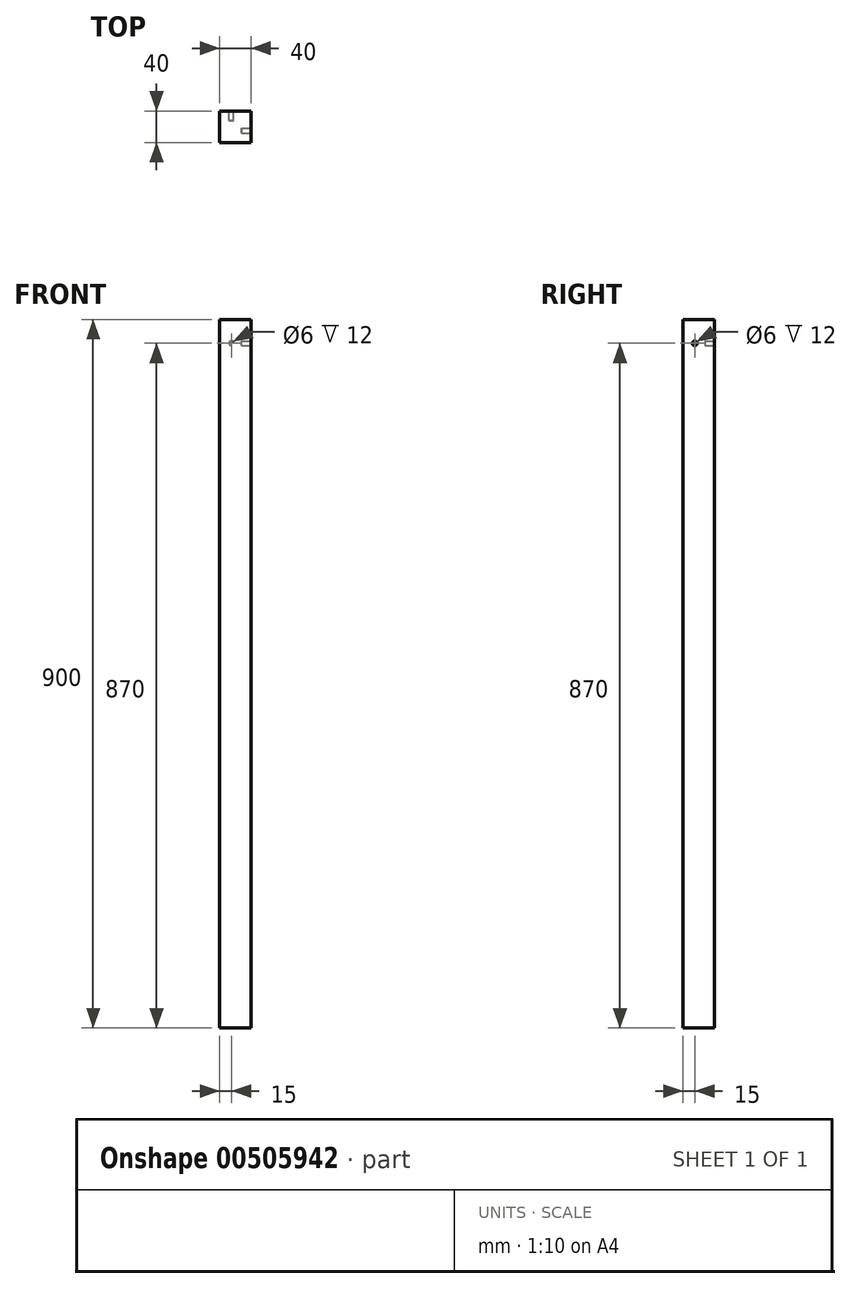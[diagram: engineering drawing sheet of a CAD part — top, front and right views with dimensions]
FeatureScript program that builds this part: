
annotation { "Feature Type Name" : "Feature", "Feature Type Description" : "" }
export const myFeature = defineFeature(function(context is Context, id is Id, definition is map)
    precondition{}
    {
        {
            var Q0;
            Q0=qCreatedBy(makeId("Top.planeOp"),FACE);
            var sketch = newSketch(context, id + "F0", { "sketchPlane" : qUnion([Q0])});
            skLineSegment(sketch, "E0.bottom", {"start": v(0, 0) * mm, "end": v(40, 0) * mm});
            skLineSegment(sketch, "E0.top", {"start": v(0, 40) * mm, "end": v(40, 40) * mm});
            skLineSegment(sketch, "E0.left", {"start": v(0, 0) * mm, "end": v(0, 40) * mm});
            skLineSegment(sketch, "E0.right", {"start": v(40, 0) * mm, "end": v(40, 40) * mm});
            skSolve(sketch);
        }
        {
            var Q0;
            Q0=makeQuery(id+"F0.imprint","IMPRINT",FACE,{"disambiguationData":[TD([[makeQuery(id+"F0.imprint","IMPRINT",EDGE,{"derivedFrom":sQuery(id+"F0.wireOp",EDGE,"E0.bottom")}),1.0]])]});
            extrude(context, id + "F1", {"entities" : qUnion([Q0]), "depth" : 900 * mm});
        }
        {
            var Q0;
            Q0=makeQuery(id+"F1.opExtrude","SWEPT_FACE",FACE,{"disambiguationData":[OSD([sQuery(id+"F0.wireOp",EDGE,"E0.right")])]});
            var sketch = newSketch(context, id + "F2", { "sketchPlane" : qUnion([Q0])});
            skCircle(sketch, "E1", {"center": v(15, 870) * mm, "radius": 3 * mm});
            skSolve(sketch);
        }
        {
            var Q0;
            Q0=makeQuery(id+"F2.imprint","IMPRINT",FACE,{"disambiguationData":[TD([[makeQuery(id+"F2.imprint","IMPRINT",EDGE,{"derivedFrom":sQuery(id+"F2.wireOp",EDGE,"E1")}),1.0]])]});
            var Q1;
            Q1=sQuery(id+"F2.wireOp",EDGE,"E1");
            extrude(context, id + "F3", {"entities" : qUnion([Q0]), "operationType" : NewBodyOperationType.REMOVE, "surfaceEntities" : qUnion([Q1]), "oppositeDirection" : true, "depth" : 12 * mm, "offsetDistance" : 25 * mm});
        }
        {
            var Q0;
            Q0=makeQuery(id+"F1.opExtrude","SWEPT_FACE",FACE,{"disambiguationData":[OSD([sQuery(id+"F0.wireOp",EDGE,"E0.top")])]});
            var sketch = newSketch(context, id + "F4", { "sketchPlane" : qUnion([Q0])});
            skCircle(sketch, "E2", {"center": v(-15, 870) * mm, "radius": 3 * mm});
            skSolve(sketch);
        }
        {
            var Q0;
            Q0=makeQuery(id+"F4.imprint","IMPRINT",FACE,{"disambiguationData":[TD([[makeQuery(id+"F4.imprint","IMPRINT",EDGE,{"derivedFrom":sQuery(id+"F4.wireOp",EDGE,"E2")}),1.0]])]});
            extrude(context, id + "F5", {"entities" : qUnion([Q0]), "operationType" : NewBodyOperationType.REMOVE, "oppositeDirection" : true, "depth" : 12 * mm, "offsetDistance" : 25 * mm});
        }
    });
